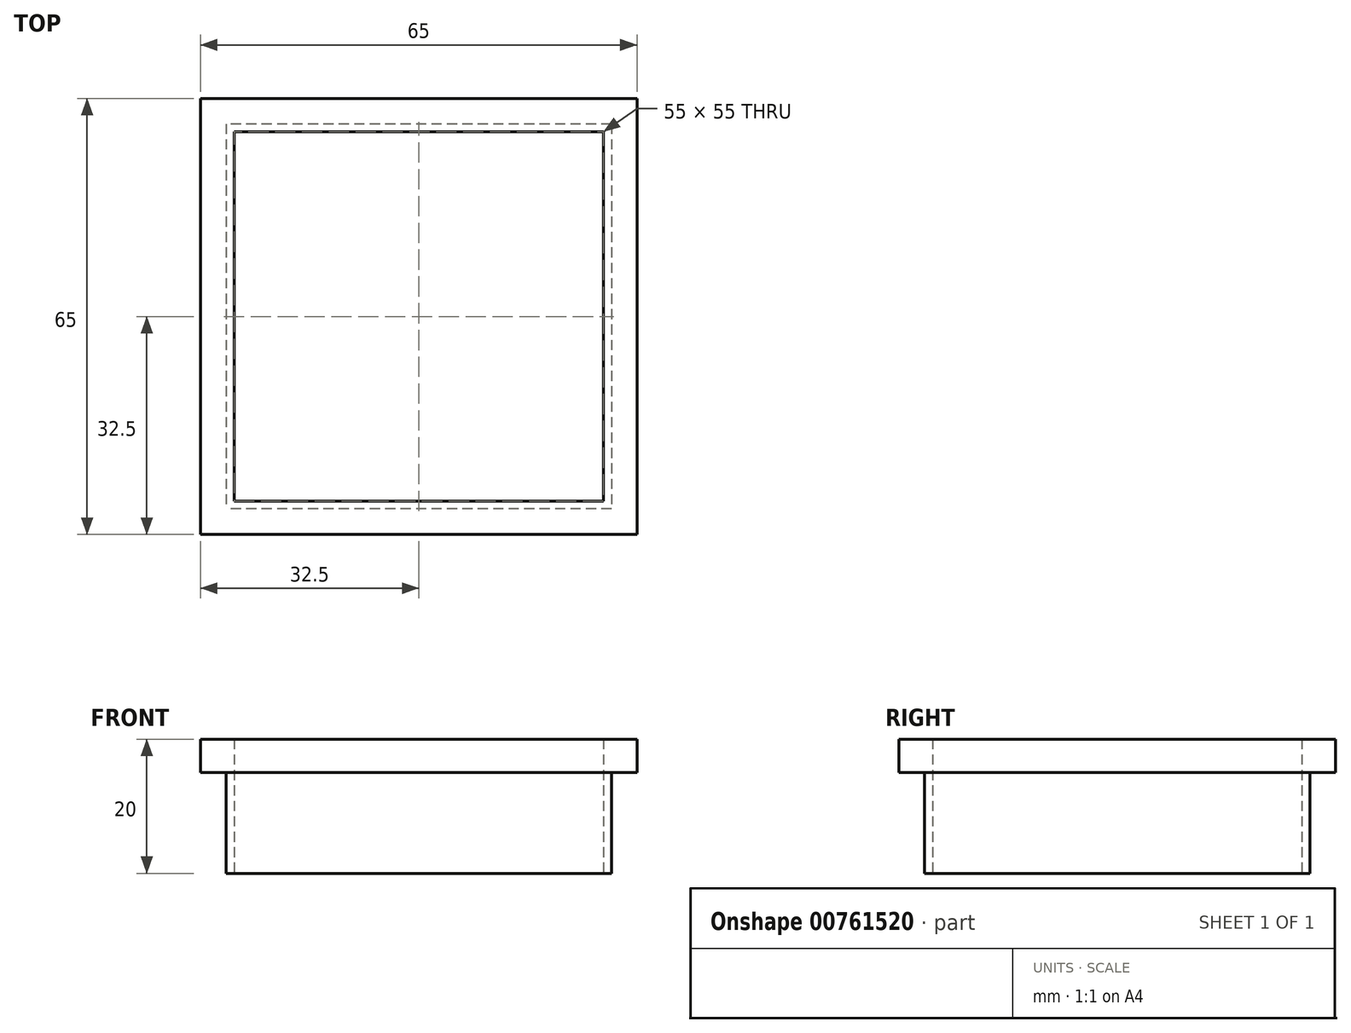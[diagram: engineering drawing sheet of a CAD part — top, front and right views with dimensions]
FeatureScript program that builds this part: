
annotation { "Feature Type Name" : "Feature", "Feature Type Description" : "" }
export const myFeature = defineFeature(function(context is Context, id is Id, definition is map)
    precondition{}
    {
        {
            var Q0;
            Q0=qCreatedBy(makeId("Top.planeOp"),FACE);
            var sketch = newSketch(context, id + "F0", { "sketchPlane" : qUnion([Q0])});
            skLineSegment(sketch, "E0.bottom", {"start": v(28.7, 28.7) * mm, "end": v(-28.7, 28.7) * mm});
            skLineSegment(sketch, "E0.top", {"start": v(28.7, -28.7) * mm, "end": v(-28.7, -28.7) * mm});
            skLineSegment(sketch, "E0.left", {"start": v(28.7, 28.7) * mm, "end": v(28.7, -28.7) * mm});
            skLineSegment(sketch, "E0.right", {"start": v(-28.7, 28.7) * mm, "end": v(-28.7, -28.7) * mm});
            skPoint(sketch, "E0.middle", {"position": v(0, 0) * mm});
            skLineSegment(sketch, "E1.bottom", {"start": v(27.5, 27.5) * mm, "end": v(-27.5, 27.5) * mm});
            skLineSegment(sketch, "E1.top", {"start": v(27.5, -27.5) * mm, "end": v(-27.5, -27.5) * mm});
            skLineSegment(sketch, "E1.left", {"start": v(27.5, 27.5) * mm, "end": v(27.5, -27.5) * mm});
            skLineSegment(sketch, "E1.right", {"start": v(-27.5, 27.5) * mm, "end": v(-27.5, -27.5) * mm});
            skSolve(sketch);
        }
        {
            var Q0;
            Q0=makeQuery(id+"F0.imprint","IMPRINT",FACE,{"disambiguationData":[TD([[makeQuery(id+"F0.imprint","IMPRINT",EDGE,{"derivedFrom":sQuery(id+"F0.wireOp",EDGE,"E0.bottom")}),1.0]])]});
            extrude(context, id + "F1", {"entities" : qUnion([Q0]), "depth" : 20 * mm, "offsetDistance" : 25 * mm});
        }
        {
            var Q0;
            Q0=makeQuery(id+"F1.opExtrude","CAP_FACE",FACE,{"disambiguationData":[OSD([sQuery(id+"F0.wireOp",EDGE,"E0.bottom"),sQuery(id+"F0.wireOp",EDGE,"E0.top"),sQuery(id+"F0.wireOp",EDGE,"E0.left"),sQuery(id+"F0.wireOp",EDGE,"E0.right"),sQuery(id+"F0.wireOp",EDGE,"E1.bottom"),sQuery(id+"F0.wireOp",EDGE,"E1.top"),sQuery(id+"F0.wireOp",EDGE,"E1.left"),sQuery(id+"F0.wireOp",EDGE,"E1.right")])],"isStart":false});
            var sketch = newSketch(context, id + "F2", { "sketchPlane" : qUnion([Q0])});
            skLineSegment(sketch, "E2.bottom", {"start": v(32.5, 32.5) * mm, "end": v(-32.5, 32.5) * mm});
            skLineSegment(sketch, "E2.top", {"start": v(32.5, -32.5) * mm, "end": v(-32.5, -32.5) * mm});
            skLineSegment(sketch, "E2.left", {"start": v(32.5, 32.5) * mm, "end": v(32.5, -32.5) * mm});
            skLineSegment(sketch, "E2.right", {"start": v(-32.5, 32.5) * mm, "end": v(-32.5, -32.5) * mm});
            skPoint(sketch, "E2.middle", {"position": v(0, 0) * mm});
            skSolve(sketch);
        }
        {
            var Q0;
            Q0=makeQuery(id+"F2.imprint","IMPRINT",FACE,{"disambiguationData":[TD([[makeQuery(id+"F2.imprint","IMPRINT",EDGE,{"derivedFrom":sQuery(id+"F2.wireOp",EDGE,"E2.bottom")}),1.0]])]});
            extrude(context, id + "F3", {"entities" : qUnion([Q0]), "operationType" : NewBodyOperationType.ADD, "oppositeDirection" : true, "depth" : 5 * mm, "offsetDistance" : 25 * mm});
        }
    });
